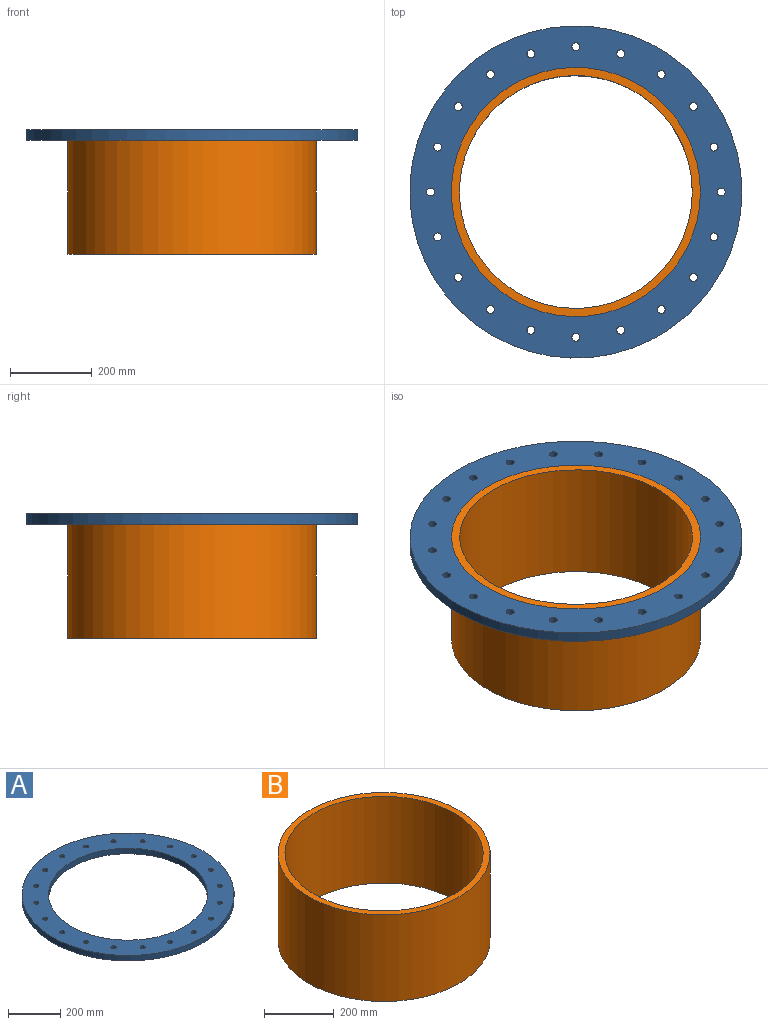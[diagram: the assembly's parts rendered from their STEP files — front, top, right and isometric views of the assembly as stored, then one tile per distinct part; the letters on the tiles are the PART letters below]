
ASSEMBLY  parts=2 mates=1
PART A: 24 faces, bbox 812.8x812.8x25.4 mm
  f0: cylinder r=304.8mm len=609.6mm, axis (0,0,-1), area 48643.9mm2, adj f2,f3
  f1: cylinder r=406.4mm len=812.8mm, axis (0,0,-1), area 64858.6mm2, adj f2,f3
  f2: plane 812.8x812.8mm, normal (0,0,1), area 221064.9mm2, adj f0,f1,f4,f5,f6,f7,f8,f9
  f3: plane 812.8x812.8mm, normal (0,0,-1), area 221064.9mm2, adj f0,f1,f4,f5,f6,f7,f8,f9
  f4: cylinder r=9.72mm len=25.4mm, axis (0,0,1), area 1551.7mm2, adj f2,f3
  f5: cylinder r=9.72mm len=25.4mm, axis (0,0,1), area 1551.7mm2, adj f2,f3
  f6: cylinder r=9.72mm len=25.4mm, axis (0,0,1), area 1551.7mm2, adj f2,f3
  f7: cylinder r=9.72mm len=25.4mm, axis (0,0,1), area 1551.7mm2, adj f2,f3
  f8: cylinder r=9.72mm len=25.4mm, axis (0,0,1), area 1551.7mm2, adj f2,f3
  f9: cylinder r=9.72mm len=25.4mm, axis (0,0,1), area 1551.7mm2, adj f2,f3
  f10: cylinder r=9.72mm len=25.4mm, axis (0,0,1), area 1551.7mm2, adj f2,f3
  f11: cylinder r=9.72mm len=25.4mm, axis (0,0,1), area 1551.7mm2, adj f2,f3
  f12: cylinder r=9.72mm len=25.4mm, axis (0,0,1), area 1551.7mm2, adj f2,f3
  f13: cylinder r=9.72mm len=25.4mm, axis (0,0,1), area 1551.7mm2, adj f2,f3
  f14: cylinder r=9.72mm len=25.4mm, axis (0,0,1), area 1551.7mm2, adj f2,f3
  f15: cylinder r=9.72mm len=25.4mm, axis (0,0,1), area 1551.7mm2, adj f2,f3
  f16: cylinder r=9.72mm len=25.4mm, axis (0,0,1), area 1551.7mm2, adj f2,f3
  f17: cylinder r=9.72mm len=25.4mm, axis (0,0,1), area 1551.7mm2, adj f2,f3
  f18: cylinder r=9.72mm len=25.4mm, axis (0,0,1), area 1551.7mm2, adj f2,f3
  f19: cylinder r=9.72mm len=25.4mm, axis (0,0,1), area 1551.7mm2, adj f2,f3
  f20: cylinder r=9.72mm len=25.4mm, axis (0,0,1), area 1551.7mm2, adj f2,f3
  f21: cylinder r=9.72mm len=25.4mm, axis (0,0,1), area 1551.7mm2, adj f2,f3
  f22: cylinder r=9.72mm len=25.4mm, axis (0,0,1), area 1551.7mm2, adj f2,f3
  f23: cylinder r=9.72mm len=25.4mm, axis (0,0,1), area 1551.7mm2, adj f2,f3
PART B: 4 faces, bbox 609.6x609.6x304.8 mm
  f0: cylinder r=284.91mm len=569.82mm, axis (0,0,-1), area 545638.8mm2, adj f2,f3
  f1: cylinder r=304.8mm len=609.6mm, axis (0,0,-1), area 583727mm2, adj f2,f3
  f2: plane 609.6x609.6mm, normal (0,0,1), area 36845.6mm2, adj f0,f1
  f3: plane 609.6x609.6mm, normal (0,0,-1), area 36845.6mm2, adj f0,f1
PLACE A t=(0,0,12.91)mm
PLACE B t=(0,0,-266.49)mm
MATE fastened A.f0 <-> B.f1  axis (0,0,1) through (0,0,38.31)mm
